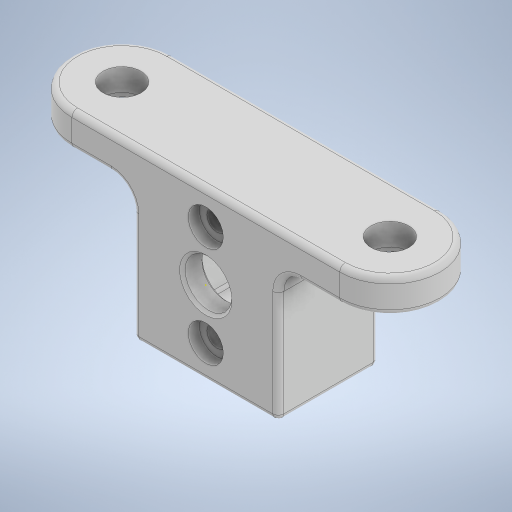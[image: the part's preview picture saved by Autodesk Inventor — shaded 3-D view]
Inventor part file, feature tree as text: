
AUTODESK INVENTOR PART (.ipt)
format: ipt  version: 2024.2 (Build 282272000, 272)  size: 381,952 bytes
history: native  units: mm
features: sketch x7, extrude x6, fillet x4, chamfer x1
ambient origin geometry x8: Origin, YZ Plane, XZ Plane, XY Plane, X Axis, Y Axis, Z Axis, Center Point
bodies: Solid1 (feature_tree)
feature tree (18):
  sketch  "Sketch1"  dims[d0=1.8mm d1=9.0mm]
  extrude  "Extrusion1"  Depth=9.0mm
  extrude  "Extrusion2"  Depth=4.5mm
  extrude  "Extrusion3"  Depth=15.0mm
  fillet  "Fillet1"  Radius=7.5mm
  fillet  "Fillet2"  Radius=6.5mm
  extrude  "Extrusion4"  Depth=1.3mm
  fillet  "Fillet3"  Radius=1.3mm
  fillet  "Fillet4"  Radius=1.3mm
  chamfer  "Chamfer1"  Distance=7.0mm
  extrude  "Extrusion5"  Depth=10.0mm
  extrude  "Extrusion6"  Depth=2.0mm
  sketch  "Sketch2"  dims[d2=4.195mm d3=4.5mm]
  sketch  "Sketch3"  dims[d4=13.0mm d5=15.0mm d6=7.5mm d7=6.5mm]
  sketch  "Sketch4"  dims[d8=2.0mm d9=0.0mm d10=1.3mm d11=1.3mm d12=1.3mm]
  sketch  "Sketch5"  dims[d13=1.3mm d14=7.0mm d15=0.0mm]
  sketch  "Sketch6"  dims[d16=3.4mm d17=10.0mm]
  sketch  "Sketch7"  dims[d18=3.0mm d19=0.0mm d20=2.0mm d21=4.5mm d22=4.5mm d23=4.5mm d24=5.25mm d25=1.0mm d26=0.0mm d27=0.5mm d28=0.25mm d29=2.0mm d30=45.0deg d31=0.25mm d32=3.15mm d33=1.0mm d34=0.0mm d35=0.2mm d36=0.0mm]
